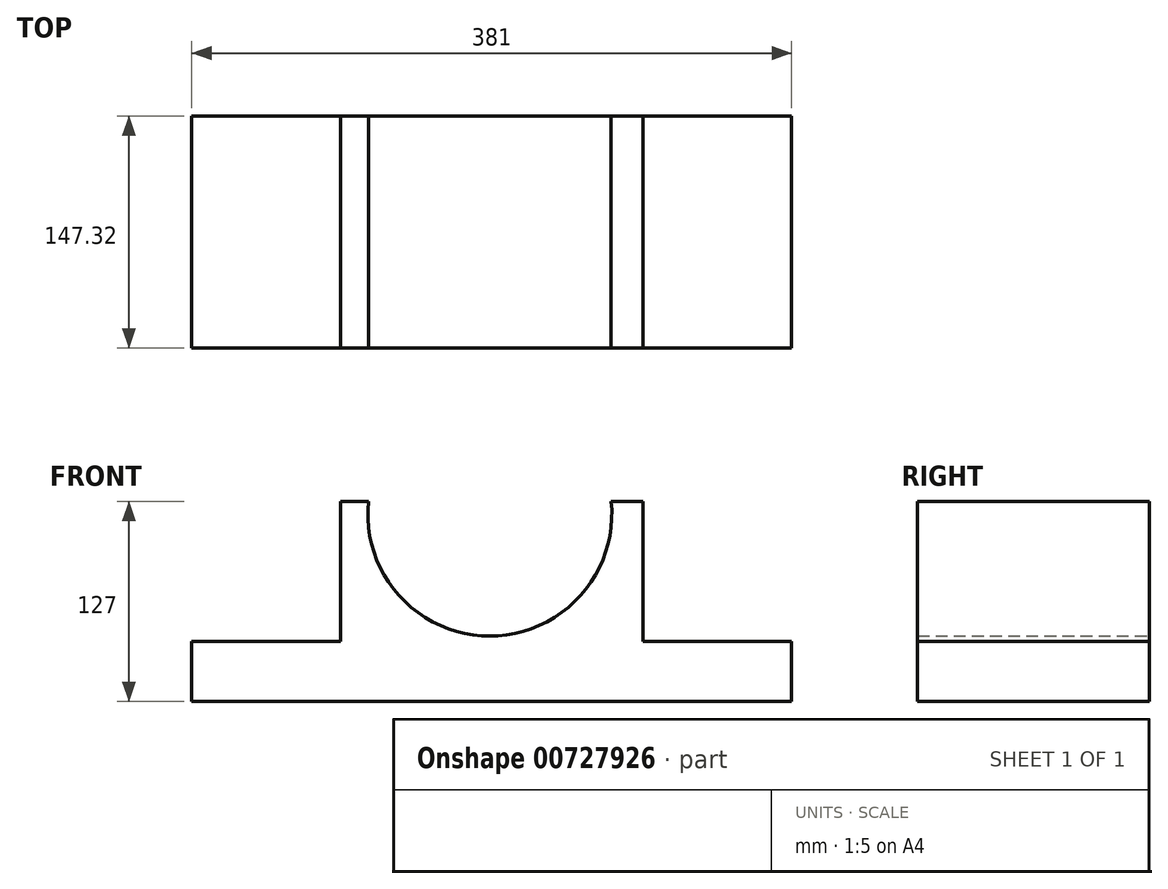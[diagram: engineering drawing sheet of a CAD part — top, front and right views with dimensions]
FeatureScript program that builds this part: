
annotation { "Feature Type Name" : "Feature", "Feature Type Description" : "" }
export const myFeature = defineFeature(function(context is Context, id is Id, definition is map)
    precondition{}
    {
        {
            var Q0;
            Q0=qCreatedBy(makeId("Front.planeOp"),FACE);
            var sketch = newSketch(context, id + "F0", { "sketchPlane" : qUnion([Q0])});
            skLineSegment(sketch, "E0", {"start": v(-48.03, 0) * mm, "end": v(332.97, 0) * mm});
            skLineSegment(sketch, "E1", {"start": v(-48.03, 0) * mm, "end": v(-48.03, 38.1) * mm});
            skLineSegment(sketch, "E2", {"start": v(332.97, 0) * mm, "end": v(332.97, 38.1) * mm});
            skLineSegment(sketch, "E3", {"start": v(-48.03, 38.1) * mm, "end": v(46.46, 38.1) * mm});
            skLineSegment(sketch, "E4", {"start": v(332.97, 38.1) * mm, "end": v(238.48, 38.1) * mm});
            skLineSegment(sketch, "E5", {"start": v(46.46, 38.1) * mm, "end": v(46.46, 127) * mm});
            skLineSegment(sketch, "E6", {"start": v(238.48, 38.1) * mm, "end": v(238.48, 127) * mm});
            skLineSegment(sketch, "E7", {"start": v(46.46, 127) * mm, "end": v(238.48, 127) * mm});
            skArc(sketch, "E8", {"start": v(64.15, 127) * mm, "mid": v(141.23, 41.55) * mm, "end": v(218.31, 127) * mm});
            skSolve(sketch);
        }
        {
            var Q0;
            Q0=makeQuery(id+"F0.imprint","IMPRINT",FACE,{"disambiguationData":[TD([[makeQuery(id+"F0.imprint","IMPRINT",EDGE,{"derivedFrom":sQuery(id+"F0.wireOp",EDGE,"E0")}),1.0]])]});
            extrude(context, id + "F1", {"entities" : qUnion([Q0]), "depth" : 147.32 * mm, "offsetDistance" : 25.4 * mm});
        }
    });
